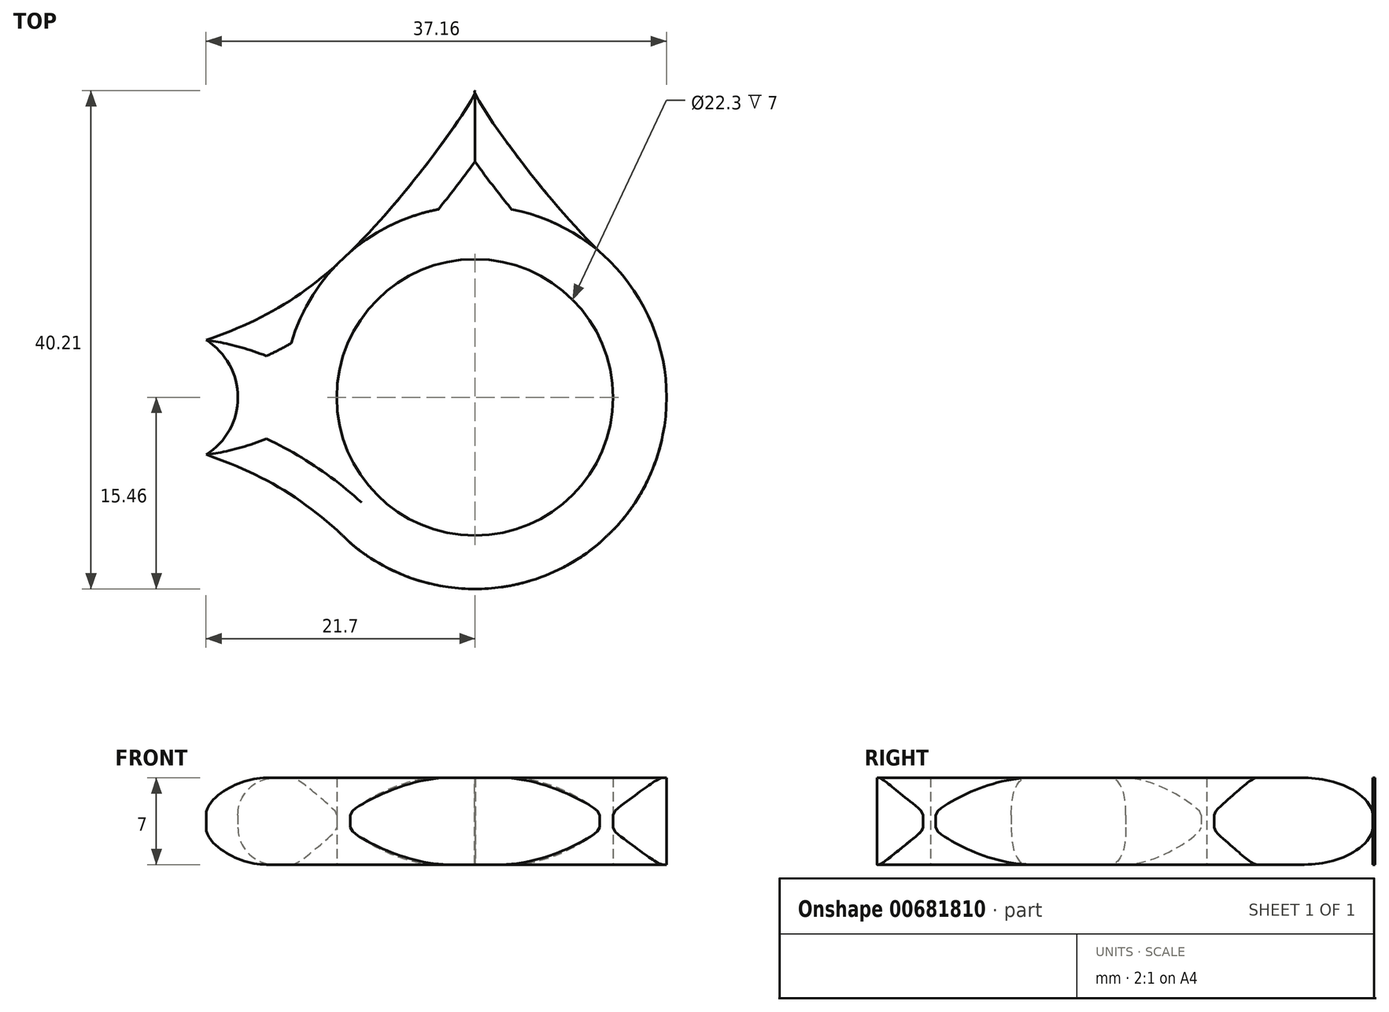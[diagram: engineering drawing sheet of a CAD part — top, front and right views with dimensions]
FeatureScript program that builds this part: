
annotation { "Feature Type Name" : "Feature", "Feature Type Description" : "" }
export const myFeature = defineFeature(function(context is Context, id is Id, definition is map)
    precondition{}
    {
        {
            var Q0;
            Q0=qCreatedBy(makeId("Top.planeOp"),FACE);
            var sketch = newSketch(context, id + "F0", { "sketchPlane" : qUnion([Q0])});
            skCircle(sketch, "E0", {"center": v(0, 0) * mm, "radius": 11.15 * mm});
            skCircle(sketch, "E1", {"center": v(0, 0) * mm, "radius": 15.46 * mm});
            skCircle(sketch, "E2", {"center": v(-24.58, 0) * mm, "radius": 3.75 * mm});
            skFitSpline(sketch, "E3", {"points": [v(-24.38, 3.74) * mm, v(-11.16, 10.71) * mm, v(0, 24.56) * mm, v(0, 24.75) * mm], "startDerivative": vector(28.12, 8.95) * mm, "endDerivative": vector(-1.1, 2.25) * mm});
            skFitSpline(sketch, "E4.MirrorCS", {"points": [v(-24.38, -3.74) * mm, v(-11.16, -10.71) * mm, v(0, -24.56) * mm, v(0, -24.75) * mm], "startDerivative": vector(28.12, -8.95) * mm, "endDerivative": vector(-1.1, -2.25) * mm});
            skCircle(sketch, "E5.MirrorC", {"center": v(24.58, 0) * mm, "radius": 3.75 * mm});
            skFitSpline(sketch, "E6.MirrorCS", {"points": [v(24.38, 3.74) * mm, v(11.16, 10.71) * mm, v(0, 24.56) * mm, v(0, 24.75) * mm], "startDerivative": vector(-28.12, 8.95) * mm, "endDerivative": vector(1.1, 2.25) * mm});
            skFitSpline(sketch, "E7.MirrorCS", {"points": [v(24.38, -3.74) * mm, v(11.16, -10.71) * mm, v(0, -24.56) * mm, v(0, -24.75) * mm], "startDerivative": vector(-28.12, -8.95) * mm, "endDerivative": vector(1.1, -2.25) * mm});
            skCircle(sketch, "E8", {"center": v(-24.58, 0) * mm, "radius": 5.45 * mm});
            skCircle(sketch, "E9.MirrorC", {"center": v(24.58, 0) * mm, "radius": 5.45 * mm});
            skSolve(sketch);
        }
        {
            var Q0;
            Q0=makeQuery(id+"F0.imprint","IMPRINT",FACE,{"disambiguationData":[TD([[makeQuery(id+"F0.imprint","IMPRINT",EDGE,{"derivedFrom":sQuery(id+"F0.wireOp",EDGE,"E0")}),-1.0]])]});
            var Q1;
            Q1=makeQuery(id+"F0.imprint","IMPRINT",FACE,{"disambiguationData":[TD([[makeQuery(id+"F0.imprint","IMPRINT",EDGE,{"derivedFrom":sQuery(id+"F0.wireOp",EDGE,"E0")}),1.0]])]});
            var Q2;
            {var subQ0=sQuery(id+"F0.wireOp",EDGE,"E2");var subQ1=sQuery(id+"F0.wireOp",EDGE,"E3");var subQ2=makeQuery(id+"F0.imprint","INTERSECT",VERTEX,{"derivedFrom":[subQ1,subQ0]});Q2=makeQuery(id+"F0.imprint","IMPRINT",FACE,{"disambiguationData":[TD([[makeQuery(id+"F0.imprint","IMPRINT",EDGE,{"disambiguationData":[TD([[subQ2,-1.0]])],"derivedFrom":subQ1}),-1.0]])]});}
            var Q3;
            {var subQ0=sQuery(id+"F0.wireOp",EDGE,"E5.MirrorC");var subQ1=sQuery(id+"F0.wireOp",EDGE,"E6.MirrorCS");var subQ2=makeQuery(id+"F0.imprint","INTERSECT",VERTEX,{"derivedFrom":[subQ1,subQ0]});Q3=makeQuery(id+"F0.imprint","IMPRINT",FACE,{"disambiguationData":[TD([[makeQuery(id+"F0.imprint","IMPRINT",EDGE,{"disambiguationData":[TD([[subQ2,-1.0]])],"derivedFrom":subQ1}),1.0]])]});}
            var Q4;
            {var subQ0=sQuery(id+"F0.wireOp",EDGE,"E2");var subQ1=sQuery(id+"F0.wireOp",EDGE,"E3");var subQ2=makeQuery(id+"F0.imprint","INTERSECT",VERTEX,{"derivedFrom":[subQ1,subQ0]});Q4=makeQuery(id+"F0.imprint","IMPRINT",FACE,{"disambiguationData":[TD([[makeQuery(id+"F0.imprint","IMPRINT",EDGE,{"disambiguationData":[TD([[subQ2,-1.0]])],"derivedFrom":subQ1}),1.0]])]});}
            var Q5;
            {var subQ0=sQuery(id+"F0.wireOp",EDGE,"E7.MirrorCS");var subQ1=sQuery(id+"F0.wireOp",EDGE,"E1");var subQ2=makeQuery(id+"F0.imprint","INTERSECT",VERTEX,{"disambiguationData":[OD(1.0)],"derivedFrom":[subQ1,subQ0]});Q5=makeQuery(id+"F0.imprint","IMPRINT",FACE,{"disambiguationData":[TD([[makeQuery(id+"F0.imprint","IMPRINT",EDGE,{"disambiguationData":[TD([[subQ2,1.0]])],"derivedFrom":subQ1}),1.0]])]});}
            var Q6;
            {var subQ0=sQuery(id+"F0.wireOp",EDGE,"E6.MirrorCS");var subQ1=sQuery(id+"F0.wireOp",EDGE,"E3");var subQ2=makeQuery(id+"F0.imprint","INTERSECT",VERTEX,{"disambiguationData":[OD(1.0)],"derivedFrom":[subQ1,subQ0]});Q6=makeQuery(id+"F0.imprint","IMPRINT",FACE,{"disambiguationData":[TD([[makeQuery(id+"F0.imprint","IMPRINT",EDGE,{"disambiguationData":[TD([[subQ2,1.0]])],"derivedFrom":subQ1}),-1.0]])]});}
            var Q7;
            {var subQ0=sQuery(id+"F0.wireOp",EDGE,"E7.MirrorCS");var subQ1=sQuery(id+"F0.wireOp",EDGE,"E1");var subQ2=makeQuery(id+"F0.imprint","INTERSECT",VERTEX,{"disambiguationData":[OD(0.0)],"derivedFrom":[subQ1,subQ0]});Q7=makeQuery(id+"F0.imprint","IMPRINT",FACE,{"disambiguationData":[TD([[makeQuery(id+"F0.imprint","IMPRINT",EDGE,{"disambiguationData":[TD([[subQ2,-1.0]])],"derivedFrom":subQ1}),1.0]])]});}
            var Q8;
            {var subQ0=sQuery(id+"F0.wireOp",EDGE,"E5.MirrorC");var subQ1=sQuery(id+"F0.wireOp",EDGE,"E6.MirrorCS");var subQ2=makeQuery(id+"F0.imprint","INTERSECT",VERTEX,{"derivedFrom":[subQ1,subQ0]});Q8=makeQuery(id+"F0.imprint","IMPRINT",FACE,{"disambiguationData":[TD([[makeQuery(id+"F0.imprint","IMPRINT",EDGE,{"disambiguationData":[TD([[subQ2,-1.0]])],"derivedFrom":subQ1}),-1.0]])]});}
            var Q9;
            {var subQ0=sQuery(id+"F0.wireOp",EDGE,"E8");var subQ1=sQuery(id+"F0.wireOp",EDGE,"E3");var subQ2=makeQuery(id+"F0.imprint","INTERSECT",VERTEX,{"derivedFrom":[subQ1,subQ0]});Q9=makeQuery(id+"F0.imprint","IMPRINT",FACE,{"disambiguationData":[TD([[makeQuery(id+"F0.imprint","IMPRINT",EDGE,{"disambiguationData":[TD([[subQ2,-1.0]])],"derivedFrom":subQ1}),-1.0]])]});}
            extrude(context, id + "F1", {"entities" : qUnion([Q0, Q1, Q2, Q3, Q4, Q5, Q6, Q7, Q8, Q9]), "depth" : 7 * mm, "offsetDistance" : 25 * mm});
        }
        {
            var Q0;
            Q0=makeQuery(id+"F1.opExtrude","CAP_EDGE",EDGE,{"disambiguationData":[OSD([sQuery(id+"F0.wireOp",EDGE,"E4.MirrorCS")])],"isStart":true});
            var Q1;
            Q1=makeQuery(id+"F1.opExtrude","CAP_EDGE",EDGE,{"disambiguationData":[OSD([sQuery(id+"F0.wireOp",EDGE,"E8")])],"isStart":true});
            var Q2;
            Q2=makeQuery(id+"F1.opExtrude","CAP_EDGE",EDGE,{"disambiguationData":[OSD([sQuery(id+"F0.wireOp",EDGE,"E3")])],"isStart":true});
            var Q3;
            Q3=makeQuery(id+"F1.opExtrude","CAP_EDGE",EDGE,{"disambiguationData":[OSD([sQuery(id+"F0.wireOp",EDGE,"E6.MirrorCS")])],"isStart":true});
            var Q4;
            Q4=makeQuery(id+"F1.opExtrude","CAP_EDGE",EDGE,{"disambiguationData":[OSD([sQuery(id+"F0.wireOp",EDGE,"E7.MirrorCS")])],"isStart":true});
            var Q5;
            Q5=makeQuery(id+"F1.opExtrude","CAP_EDGE",EDGE,{"disambiguationData":[OSD([sQuery(id+"F0.wireOp",EDGE,"E9.MirrorC")])],"isStart":true});
            var Q6;
            Q6=makeQuery(id+"F1.opExtrude","CAP_EDGE",EDGE,{"disambiguationData":[OSD([sQuery(id+"F0.wireOp",EDGE,"E7.MirrorCS")])],"isStart":false});
            var Q7;
            Q7=makeQuery(id+"F1.opExtrude","CAP_EDGE",EDGE,{"disambiguationData":[OSD([sQuery(id+"F0.wireOp",EDGE,"E4.MirrorCS")])],"isStart":false});
            var Q8;
            Q8=makeQuery(id+"F1.opExtrude","CAP_EDGE",EDGE,{"disambiguationData":[OSD([sQuery(id+"F0.wireOp",EDGE,"E8")])],"isStart":false});
            var Q9;
            Q9=makeQuery(id+"F1.opExtrude","CAP_EDGE",EDGE,{"disambiguationData":[OSD([sQuery(id+"F0.wireOp",EDGE,"E3")])],"isStart":false});
            var Q10;
            Q10=makeQuery(id+"F1.opExtrude","CAP_EDGE",EDGE,{"disambiguationData":[OSD([sQuery(id+"F0.wireOp",EDGE,"E6.MirrorCS")])],"isStart":false});
            var Q11;
            Q11=makeQuery(id+"F1.opExtrude","CAP_EDGE",EDGE,{"disambiguationData":[OSD([sQuery(id+"F0.wireOp",EDGE,"E9.MirrorC")])],"isStart":false});
            fillet(context, id + "F2", {"entities" : qUnion([Q0, Q1, Q2, Q3, Q4, Q5, Q6, Q7, Q8, Q9, Q10, Q11]), "radius" : 3 * mm, "tangentPropagation" : true, "allowEdgeOverflow" : false});
        }
    });
